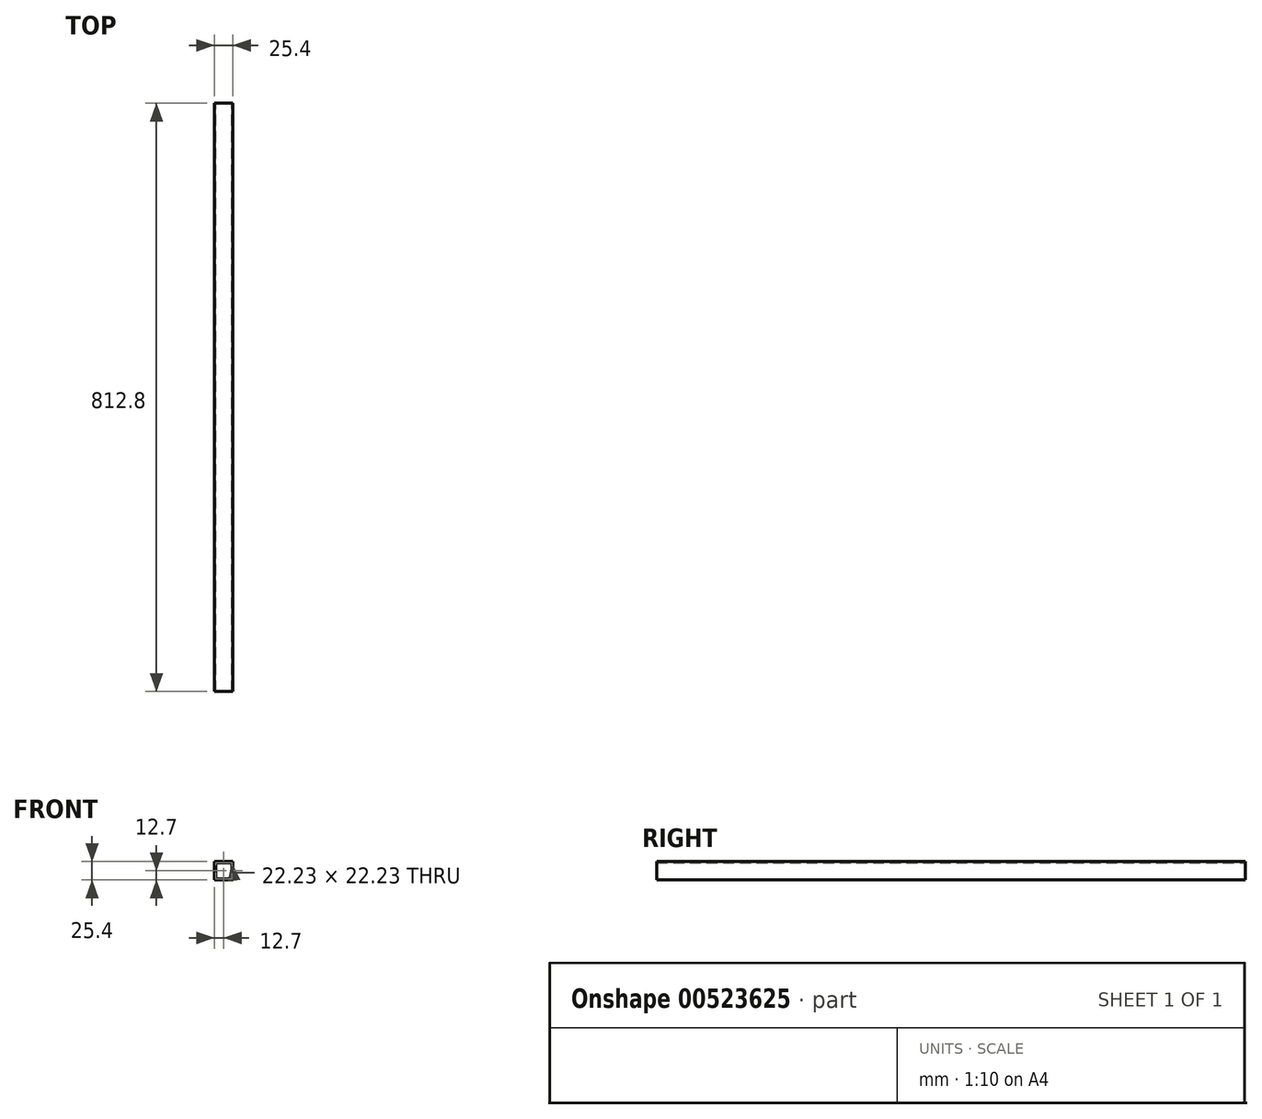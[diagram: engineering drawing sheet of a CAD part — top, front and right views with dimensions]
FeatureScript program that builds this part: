
annotation { "Feature Type Name" : "Feature", "Feature Type Description" : "" }
export const myFeature = defineFeature(function(context is Context, id is Id, definition is map)
    precondition{}
    {
        {
            var Q0;
            Q0=qCreatedBy(makeId("Front.planeOp"),FACE);
            var sketch = newSketch(context, id + "F0", { "sketchPlane" : qUnion([Q0])});
            skLineSegment(sketch, "E0.bottom", {"start": v(-12.7, -12.7) * mm, "end": v(12.7, -12.7) * mm});
            skLineSegment(sketch, "E0.top", {"start": v(-12.7, 12.7) * mm, "end": v(12.7, 12.7) * mm});
            skLineSegment(sketch, "E0.left", {"start": v(-12.7, -12.7) * mm, "end": v(-12.7, 12.7) * mm});
            skLineSegment(sketch, "E0.right", {"start": v(12.7, -12.7) * mm, "end": v(12.7, 12.7) * mm});
            skLineSegment(sketch, "E1.bottom", {"start": v(-11.11, -11.11) * mm, "end": v(11.11, -11.11) * mm});
            skLineSegment(sketch, "E1.top", {"start": v(-11.11, 11.11) * mm, "end": v(11.11, 11.11) * mm});
            skLineSegment(sketch, "E1.left", {"start": v(-11.11, -11.11) * mm, "end": v(-11.11, 11.11) * mm});
            skLineSegment(sketch, "E1.right", {"start": v(11.11, -11.11) * mm, "end": v(11.11, 11.11) * mm});
            skLineSegment(sketch, "E2", {"start": v(-11.11, 0) * mm, "end": v(11.11, 0) * mm, "construction": true});
            skLineSegment(sketch, "E3", {"start": v(0, 12.7) * mm, "end": v(0, -12.7) * mm, "construction": true});
            skSolve(sketch);
        }
        {
            var Q0;
            Q0 = qSketchRegion(id + "F0", true);
            extrude(context, id + "F1", {"entities" : qUnion([Q0]), "endBound" : BoundingType.SYMMETRIC, "depth" : 812.8 * mm, "offsetDistance" : 25.4 * mm});
        }
    });
